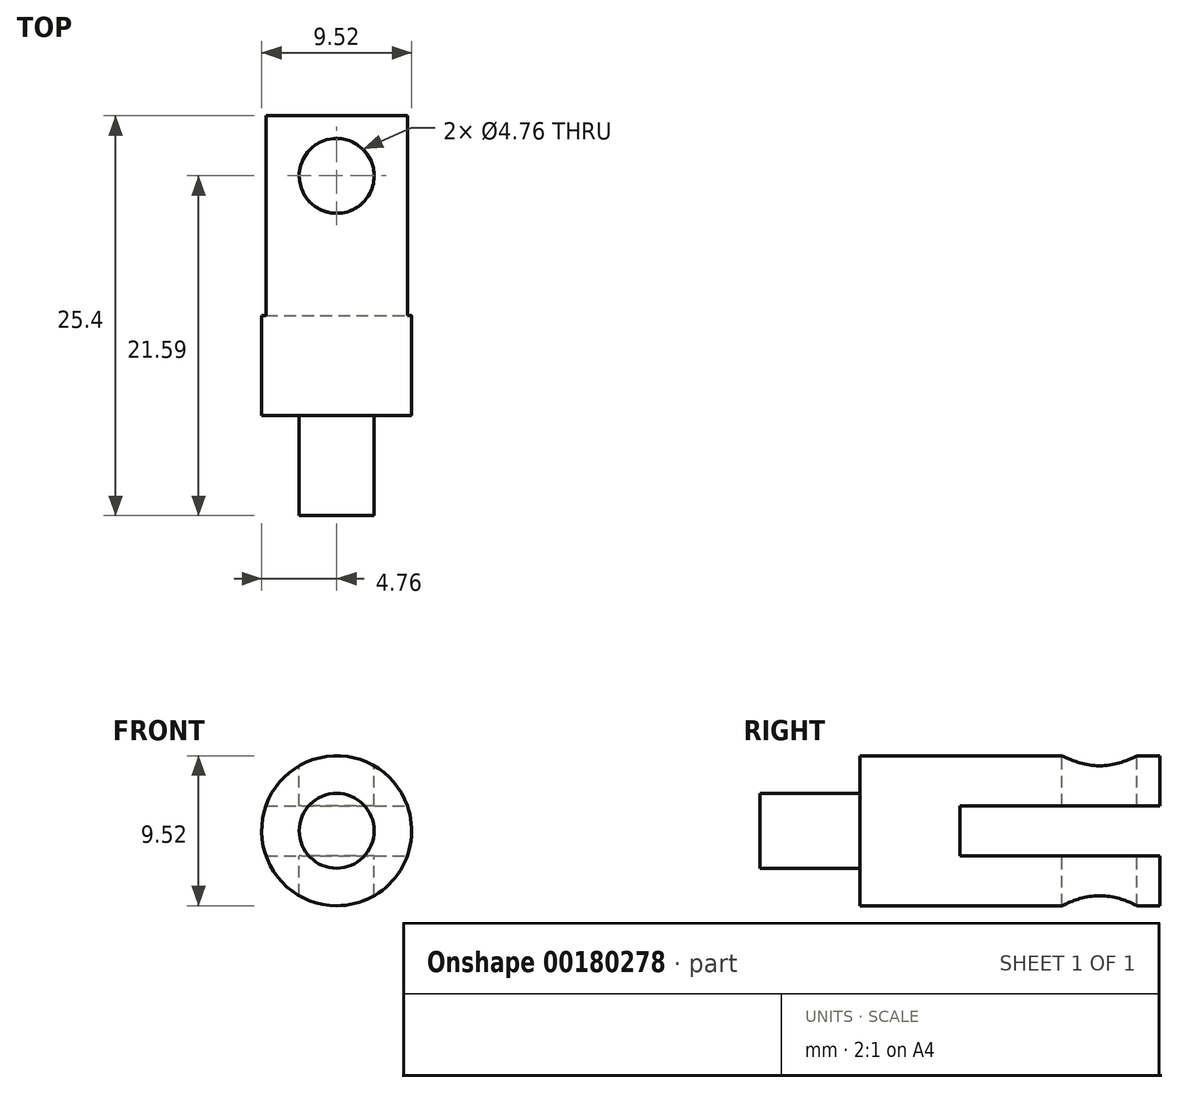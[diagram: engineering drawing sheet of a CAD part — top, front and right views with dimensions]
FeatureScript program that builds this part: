
annotation { "Feature Type Name" : "Feature", "Feature Type Description" : "" }
export const myFeature = defineFeature(function(context is Context, id is Id, definition is map)
    precondition{}
    {
        {
            var Q0;
            Q0=qCreatedBy(makeId("Front.planeOp"),FACE);
            var sketch = newSketch(context, id + "F0", { "sketchPlane" : qUnion([Q0])});
            skCircle(sketch, "E0", {"center": v(0, 0) * mm, "radius": 4.76 * mm});
            skSolve(sketch);
        }
        {
            var Q0;
            Q0 = qSketchRegion(id + "F0", true);
            extrude(context, id + "F1", {"entities" : qUnion([Q0]), "depth" : 25.4 * mm});
        }
        {
            var Q0;
            Q0=qCreatedBy(makeId("Right.planeOp"),FACE);
            var sketch = newSketch(context, id + "F2", { "sketchPlane" : qUnion([Q0])});
            skLineSegment(sketch, "E1.bottom", {"start": v(-19.05, 7.12) * mm, "end": v(-25.4, 7.12) * mm});
            skLineSegment(sketch, "E1.top", {"start": v(-19.05, 2.38) * mm, "end": v(-25.4, 2.38) * mm});
            skLineSegment(sketch, "E1.left", {"start": v(-19.05, 7.12) * mm, "end": v(-19.05, 2.38) * mm});
            skLineSegment(sketch, "E1.right", {"start": v(-25.4, 7.12) * mm, "end": v(-25.4, 2.38) * mm});
            skLineSegment(sketch, "E2", {"start": v(0, 0) * mm, "end": v(-50.7, 0) * mm, "construction": true});
            skSolve(sketch);
        }
        {
            var Q0;
            Q0=makeQuery(id+"F2.imprint","IMPRINT",FACE,{"disambiguationData":[TD([[makeQuery(id+"F2.imprint","IMPRINT",EDGE,{"derivedFrom":sQuery(id+"F2.wireOp",EDGE,"E1.bottom")}),1.0]])]});
            var Q1;
            Q1=sQuery(id+"F2.wireOp",EDGE,"E1.top");
            var Q2;
            Q2=sQuery(id+"F2.wireOp",EDGE,"E1.left");
            var Q3;
            Q3=sQuery(id+"F2.wireOp",EDGE,"E1.right");
            var Q4;
            Q4=sQuery(id+"F2.wireOp",EDGE,"E1.bottom");
            var Q5;
            Q5=sQuery(id+"F2.wireOp",EDGE,"E2");
            revolve(context, id + "F3", {"operationType" : NewBodyOperationType.REMOVE, "entities" : qUnion([Q0]), "surfaceEntities" : qUnion([Q1, Q2, Q3, Q4]), "axis" : qUnion([Q5]), "revolveType" : RevolveType.FULL});
        }
        {
            var Q0;
            Q0=qCreatedBy(makeId("Right.planeOp"),FACE);
            var sketch = newSketch(context, id + "F4", { "sketchPlane" : qUnion([Q0])});
            skLineSegment(sketch, "E3", {"start": v(0, 0) * mm, "end": v(0, 1.59) * mm});
            skLineSegment(sketch, "E4", {"start": v(0, 1.59) * mm, "end": v(-12.7, 1.59) * mm});
            skLineSegment(sketch, "E5", {"start": v(-12.7, 1.59) * mm, "end": v(-12.7, 0) * mm});
            skLineSegment(sketch, "E6.MirrorCS", {"start": v(-12.7, -1.59) * mm, "end": v(-12.7, 0) * mm});
            skLineSegment(sketch, "E7.MirrorCS", {"start": v(0, 0) * mm, "end": v(0, -1.59) * mm});
            skLineSegment(sketch, "E8.MirrorCS", {"start": v(0, -1.59) * mm, "end": v(-12.7, -1.59) * mm});
            skLineSegment(sketch, "E9.bottom", {"start": v(0, 3.18) * mm, "end": v(-12.7, 3.17) * mm});
            skLineSegment(sketch, "E9.top", {"start": v(0, 5.53) * mm, "end": v(-12.7, 5.53) * mm});
            skLineSegment(sketch, "E9.left", {"start": v(0, 3.18) * mm, "end": v(0, 5.53) * mm});
            skLineSegment(sketch, "E9.right", {"start": v(-12.7, 3.17) * mm, "end": v(-12.7, 5.53) * mm});
            skLineSegment(sketch, "E10.MirrorCS", {"start": v(-12.7, -3.17) * mm, "end": v(-12.7, -5.53) * mm});
            skLineSegment(sketch, "E11.MirrorCS", {"start": v(0, -3.18) * mm, "end": v(0, -5.53) * mm});
            skLineSegment(sketch, "E12.MirrorCS", {"start": v(0, -3.18) * mm, "end": v(-12.7, -3.17) * mm});
            skLineSegment(sketch, "E13.MirrorCS", {"start": v(0, -5.53) * mm, "end": v(-12.7, -5.53) * mm});
            skSolve(sketch);
        }
        {
            var Q0;
            Q0=makeQuery(id+"F4.imprint","IMPRINT",FACE,{"disambiguationData":[TD([[makeQuery(id+"F4.imprint","IMPRINT",EDGE,{"derivedFrom":sQuery(id+"F4.wireOp",EDGE,"E3")}),1.0]])]});
            extrude(context, id + "F5", {"entities" : qUnion([Q0]), "operationType" : NewBodyOperationType.REMOVE, "endBound" : BoundingType.THROUGH_ALL, "oppositeDirection" : true, "depth" : 25.4 * mm, "hasSecondDirection" : true, "secondDirectionBound" : SecondDirectionBoundingType.THROUGH_ALL, "secondDirectionOppositeDirection" : false, "secondDirectionDepth" : 25.4 * mm});
        }
        {
            var Q0;
            Q0=qCreatedBy(makeId("Top.planeOp"),FACE);
            var sketch = newSketch(context, id + "F6", { "sketchPlane" : qUnion([Q0])});
            skCircle(sketch, "E14", {"center": v(0, -3.81) * mm, "radius": 2.38 * mm});
            skSolve(sketch);
        }
        {
            var Q0;
            Q0 = qSketchRegion(id + "F6", true);
            extrude(context, id + "F7", {"entities" : qUnion([Q0]), "operationType" : NewBodyOperationType.REMOVE, "endBound" : BoundingType.SYMMETRIC, "oppositeDirection" : true, "depth" : 25.4 * mm, "hasSecondDirection" : true, "secondDirectionBound" : SecondDirectionBoundingType.UP_TO_SURFACE, "secondDirectionOppositeDirection" : false, "secondDirectionDepth" : 25.4 * mm});
        }
    });
